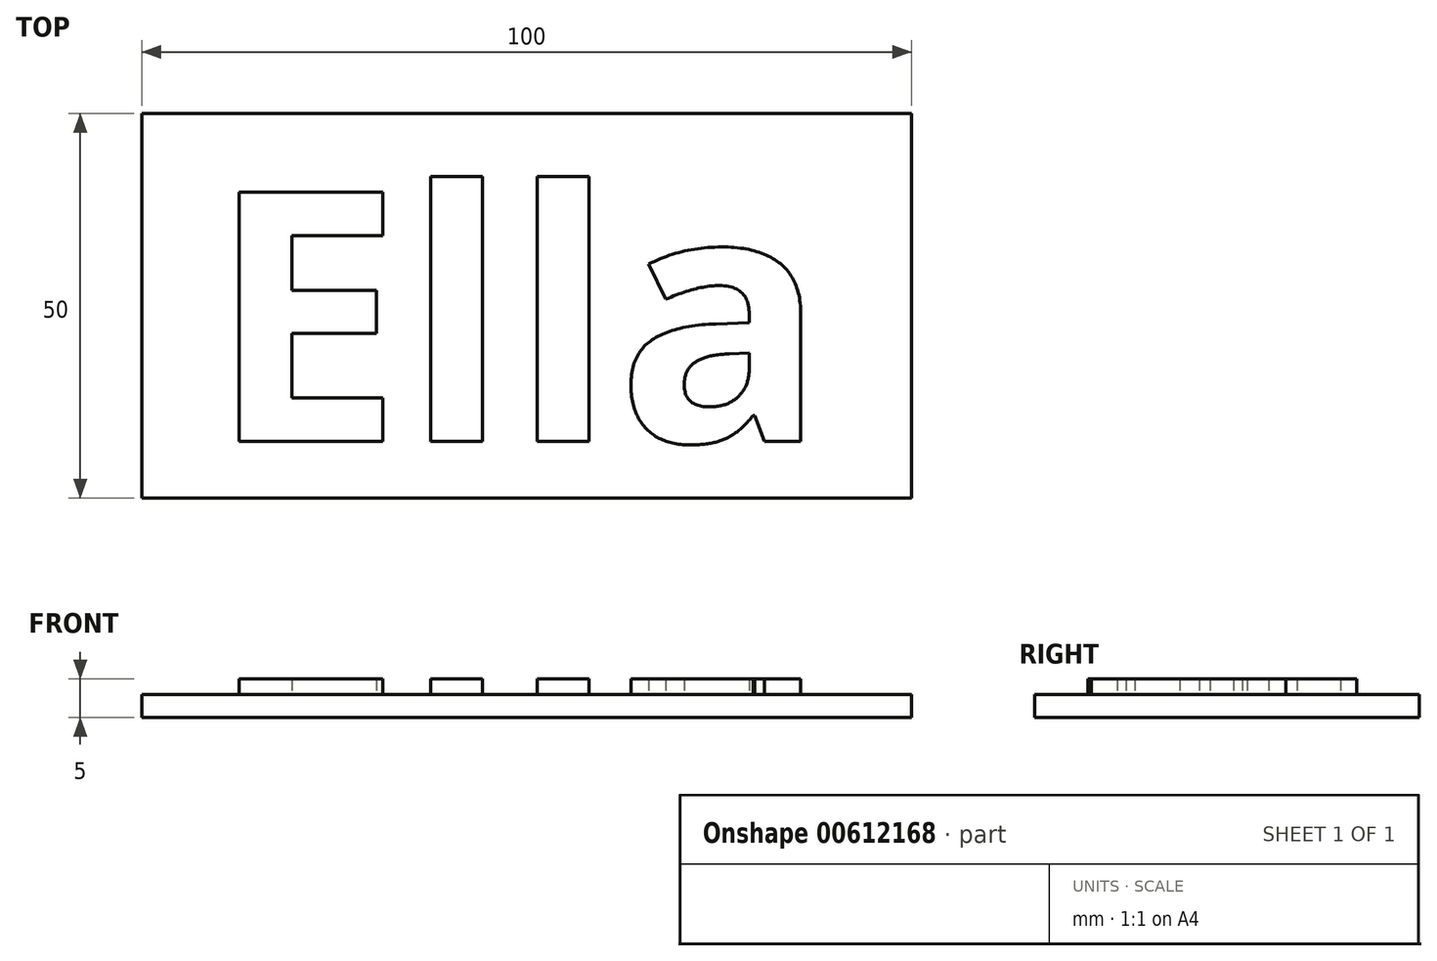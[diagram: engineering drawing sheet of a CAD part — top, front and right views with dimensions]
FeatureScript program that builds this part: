
annotation { "Feature Type Name" : "Feature", "Feature Type Description" : "" }
export const myFeature = defineFeature(function(context is Context, id is Id, definition is map)
    precondition{}
    {
        {
            var Q0;
            Q0=qCreatedBy(makeId("Top.planeOp"),FACE);
            var sketch = newSketch(context, id + "F0", { "sketchPlane" : qUnion([Q0])});
            skLineSegment(sketch, "E0.bottom", {"start": v(0, 0) * mm, "end": v(-100, 0) * mm});
            skLineSegment(sketch, "E0.top", {"start": v(0, 50) * mm, "end": v(-100, 50) * mm});
            skLineSegment(sketch, "E0.left", {"start": v(0, 0) * mm, "end": v(0, 50) * mm});
            skLineSegment(sketch, "E0.right", {"start": v(-100, 0) * mm, "end": v(-100, 50) * mm});
            skSolve(sketch);
        }
        {
            var Q0;
            Q0 = qSketchRegion(id + "F0", true);
            extrude(context, id + "F1", {"entities" : qUnion([Q0]), "depth" : 3 * mm, "offsetDistance" : 25 * mm});
        }
        {
            var Q0;
            Q0=makeQuery(id+"F1.opExtrude","CAP_FACE",FACE,{"disambiguationData":[OSD([sQuery(id+"F0.wireOp",EDGE,"E0.bottom"),sQuery(id+"F0.wireOp",EDGE,"E0.top"),sQuery(id+"F0.wireOp",EDGE,"E0.left"),sQuery(id+"F0.wireOp",EDGE,"E0.right")])],"isStart":false});
            var sketch = newSketch(context, id + "F2", { "sketchPlane" : qUnion([Q0])});
            skSolve(sketch);
        }
        {
            var Q0;
            Q0=makeQuery(id+"F1.opExtrude","CAP_FACE",FACE,{"disambiguationData":[OSD([sQuery(id+"F0.wireOp",EDGE,"E0.bottom"),sQuery(id+"F0.wireOp",EDGE,"E0.top"),sQuery(id+"F0.wireOp",EDGE,"E0.left"),sQuery(id+"F0.wireOp",EDGE,"E0.right")])],"isStart":false});
            var sketch = newSketch(context, id + "F3", { "sketchPlane" : qUnion([Q0])});
            skText(sketch, "E1", { "text": "Ella", "fontName": "NotoSans-Bold.ttf"});
            const initialGuessF3  = {"E1": [-0.09143, 0.00737, 1, 0, 0.03265]};
            skSetInitialGuess(sketch, initialGuessF3);
            skSolve(sketch);
        }
        {
            var Q0;
            Q0=makeQuery(id+"F2.imprint","IMPRINT",FACE,{"disambiguationData":[TD([[makeQuery(id+"F2.imprint","IMPRINT",EDGE,{"derivedFrom":makeQuery(id+"F1.opExtrude","CAP_EDGE",EDGE,{"disambiguationData":[OSD([sQuery(id+"F0.wireOp",EDGE,"E0.bottom")])],"isStart":false})}),-1.0]])]});
            var Q1;
            Q1 = qSketchRegion(id + "F3", true);
            extrude(context, id + "F4", {"entities" : qUnion([Q0, Q1]), "operationType" : NewBodyOperationType.ADD, "depth" : 2 * mm, "offsetDistance" : 25 * mm});
        }
        {
            var Q0;
            Q0 = qSketchRegion(id + "F3", true);
            extrude(context, id + "F5", {"entities" : qUnion([Q0]), "operationType" : NewBodyOperationType.ADD, "depth" : 2 * mm, "offsetDistance" : 25 * mm});
        }
        {
            var Q0;
            Q0 = qSketchRegion(id + "F3", true);
            extrude(context, id + "F6", {"entities" : qUnion([Q0]), "operationType" : NewBodyOperationType.ADD, "depth" : 2 * mm, "offsetDistance" : 25 * mm});
        }
        {
            var Q0;
            Q0 = qSketchRegion(id + "F3", true);
            var Q1;
            Q1=makeQuery(id+"F4.opExtrude","CAP_FACE",FACE,{"disambiguationData":[OSD([sQuery(id+"F0.wireOp",EDGE,"E0.bottom"),sQuery(id+"F0.wireOp",EDGE,"E0.top"),sQuery(id+"F0.wireOp",EDGE,"E0.left"),sQuery(id+"F0.wireOp",EDGE,"E0.right")])],"isStart":false});
            extrude(context, id + "F7", {"entities" : qUnion([Q0, Q1]), "operationType" : NewBodyOperationType.ADD, "depth" : 2 * mm, "offsetDistance" : 25 * mm});
        }
        {
            var Q0;
            Q0 = qSketchRegion(id + "F3", true);
            var Q1;
            Q1=makeQuery(id+"F7.opExtrude","CAP_FACE",FACE,{"disambiguationData":[OSD([sQuery(id+"F0.wireOp",EDGE,"E0.bottom"),sQuery(id+"F0.wireOp",EDGE,"E0.top"),sQuery(id+"F0.wireOp",EDGE,"E0.left"),sQuery(id+"F0.wireOp",EDGE,"E0.right")])],"isStart":false});
            extrude(context, id + "F8", {"entities" : qUnion([Q0, Q1]), "operationType" : NewBodyOperationType.ADD, "depth" : 2 * mm, "offsetDistance" : 25 * mm});
        }
    });
